# Revit family: Intersan Solidwave Classic
name_source: partatom
category: Plumbing Fixtures
revit_build: Autodesk Revit 2017 (Build: 20170816_0615(x64)
units: mm (PartAtom-declared; Revit-internal decimal feet)

## family parameters
Always vertical = Yes
Cut with Voids When Loaded = No
OmniClass Number = 23.45.05.14.14
OmniClass Title = Sinks/Lavatories
Part Type = Normal
Room Calculation Point = No
Round Connector Dimension = Use Diameter
Shared = No
Work Plane-Based = No

## types (3) — shared parameters
Apron Height = 6 3/8"
CW Connection = Yes
Drain Diameter = 1 1/2"
HW Connection = Yes
Manufacturer = Intersan
Material = Anti-microbial Solid Surface and Stainless Steel
Model = Solidwave Classic
Standard Conformance = CSA B45.5-11/IAPMO Z124-2011 - IAPMO IGC156
Supply Cold Diameter = 1/2"
Supply Hot Diameter = 1/2"
Unit Depth = 21 1/2"
Unit Height = 23 1/8"
Warranty = 5 years on material - 1 year on faucets
Waste Connection = Yes
Water Usage = 0.35 gpm/user if Intersan Faucets

## per-type parameters (varying)
| type | Unit Width |
| 1-user | 30" |
| 2-user | 60" |
| 3-user | 90" |

## geometry (parser evidence)
native form markers: Sweep x3
no freeform markers — native parametric forms only
